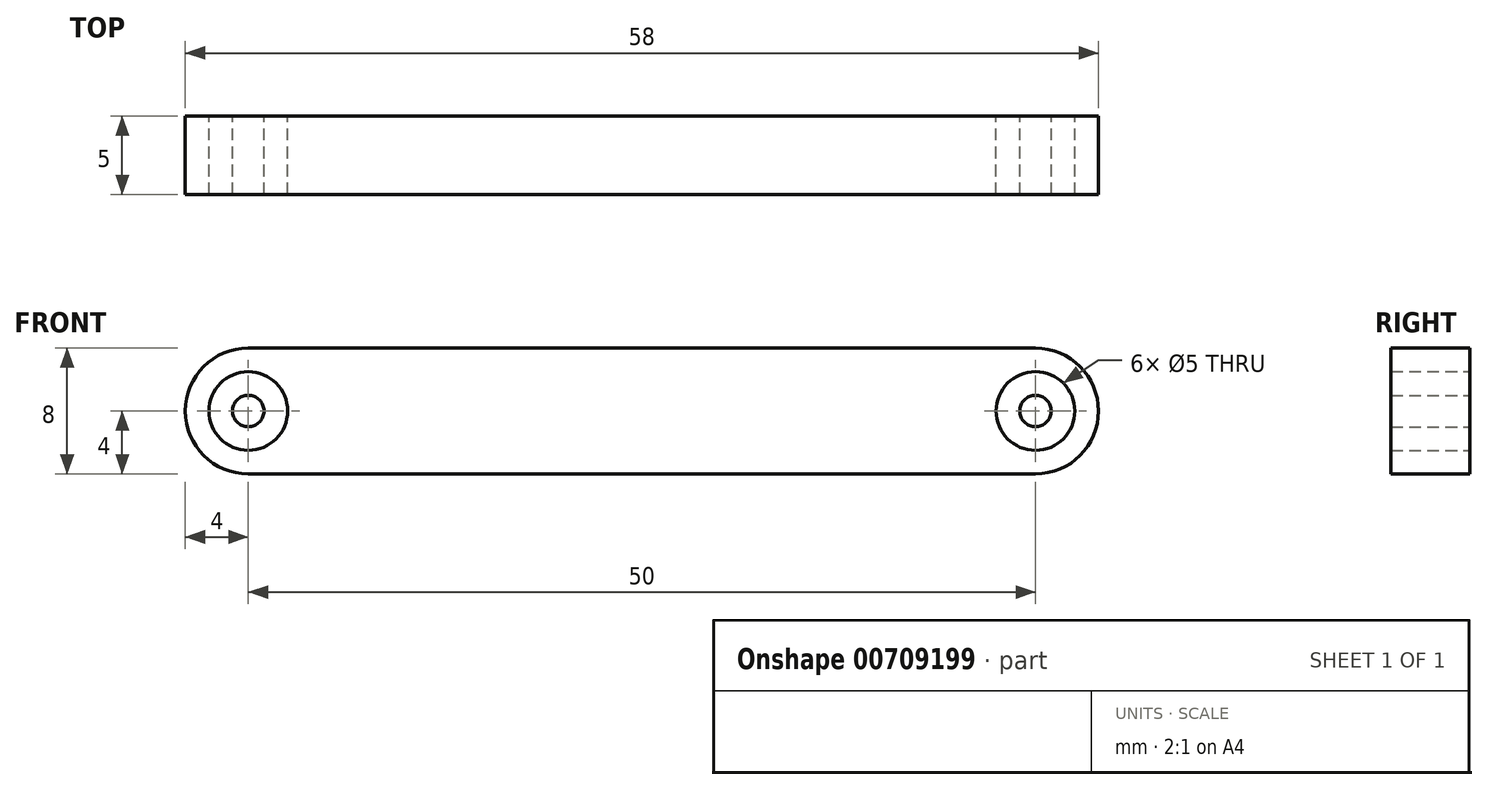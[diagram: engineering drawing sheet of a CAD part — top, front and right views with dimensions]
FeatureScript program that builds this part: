
annotation { "Feature Type Name" : "Feature", "Feature Type Description" : "" }
export const myFeature = defineFeature(function(context is Context, id is Id, definition is map)
    precondition{}
    {
        {
            var Q0;
            Q0=qCreatedBy(makeId("Front.planeOp"),FACE);
            var sketch = newSketch(context, id + "F0", { "sketchPlane" : qUnion([Q0])});
            skArc(sketch, "E0", {"start": v(0, 4) * mm, "mid": v(-4, 0) * mm, "end": v(0, -4) * mm});
            skArc(sketch, "E1", {"start": v(50, -4) * mm, "mid": v(54, 0) * mm, "end": v(50, 4) * mm});
            skLineSegment(sketch, "E2", {"start": v(0, 4) * mm, "end": v(50, 4) * mm});
            skLineSegment(sketch, "E3", {"start": v(0, -4) * mm, "end": v(50, -4) * mm});
            skCircle(sketch, "E4", {"center": v(0, 0) * mm, "radius": 2.5 * mm});
            skCircle(sketch, "E5", {"center": v(0, 0) * mm, "radius": 1 * mm});
            skCircle(sketch, "E6", {"center": v(50, 0) * mm, "radius": 2.5 * mm});
            skCircle(sketch, "E7", {"center": v(50, 0) * mm, "radius": 1 * mm});
            skSolve(sketch);
        }
        {
            var Q0;
            Q0=makeQuery(id+"F0.imprint","IMPRINT",FACE,{"disambiguationData":[TD([[makeQuery(id+"F0.imprint","IMPRINT",EDGE,{"derivedFrom":sQuery(id+"F0.wireOp",EDGE,"E0")}),1.0]])]});
            var Q1;
            Q1=makeQuery(id+"F0.imprint","IMPRINT",FACE,{"disambiguationData":[TD([[makeQuery(id+"F0.imprint","IMPRINT",EDGE,{"derivedFrom":sQuery(id+"F0.wireOp",EDGE,"E5")}),1.0]])]});
            var Q2;
            Q2=makeQuery(id+"F0.imprint","IMPRINT",FACE,{"disambiguationData":[TD([[makeQuery(id+"F0.imprint","IMPRINT",EDGE,{"derivedFrom":sQuery(id+"F0.wireOp",EDGE,"E7")}),1.0]])]});
            extrude(context, id + "F1", {"entities" : qUnion([Q0, Q1, Q2]), "depth" : 5 * mm, "offsetDistance" : 25 * mm});
        }
    });
